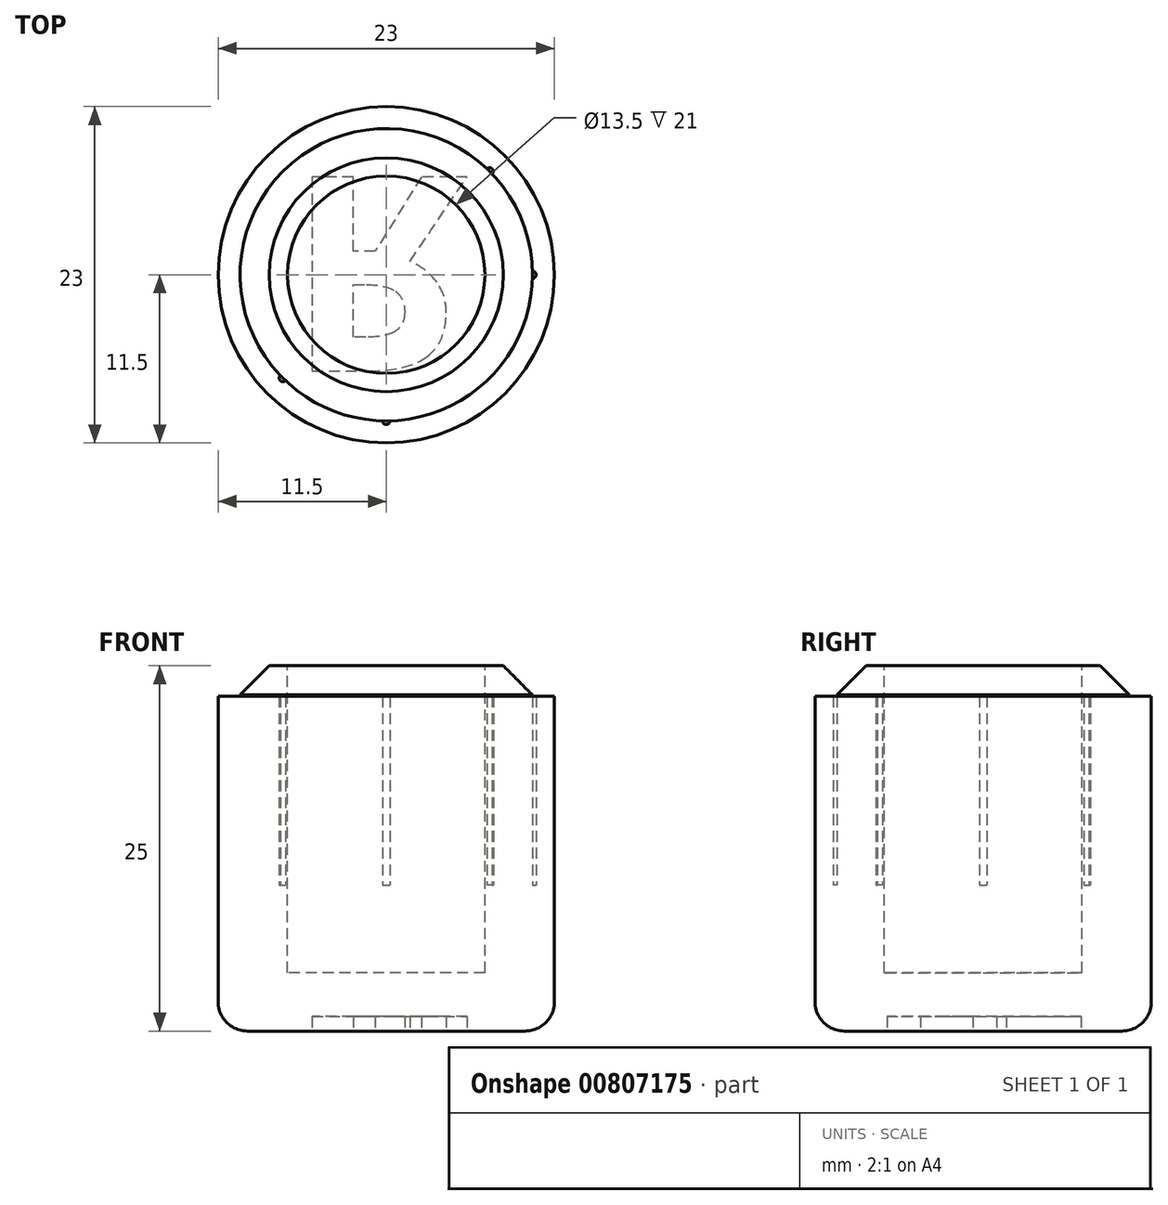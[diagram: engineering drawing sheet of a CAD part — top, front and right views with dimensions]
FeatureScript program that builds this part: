
annotation { "Feature Type Name" : "Feature", "Feature Type Description" : "" }
export const myFeature = defineFeature(function(context is Context, id is Id, definition is map)
    precondition{}
    {
        {
            var Q0;
            Q0=qCreatedBy(makeId("Top.planeOp"),FACE);
            var sketch = newSketch(context, id + "F0", { "sketchPlane" : qUnion([Q0])});
            skCircle(sketch, "E0", {"center": v(0, 0) * mm, "radius": 11.5 * mm});
            skSolve(sketch);
        }
        {
            var Q0;
            Q0 = qSketchRegion(id + "F0", true);
            extrude(context, id + "F1", {"entities" : qUnion([Q0]), "depth" : 10 * mm, "offsetDistance" : 25 * mm});
        }
        {
            var Q0;
            Q0=makeQuery(id+"F1.opExtrude","CAP_FACE",FACE,{"disambiguationData":[OSD([sQuery(id+"F0.wireOp",EDGE,"E0")])],"isStart":false});
            var sketch = newSketch(context, id + "F2", { "sketchPlane" : qUnion([Q0])});
            skCircle(sketch, "E1", {"center": v(0, 0) * mm, "radius": 6.75 * mm});
            skSolve(sketch);
        }
        {
            var Q0;
            Q0 = qSketchRegion(id + "F2", true);
            extrude(context, id + "F3", {"entities" : qUnion([Q0]), "operationType" : NewBodyOperationType.REMOVE, "oppositeDirection" : true, "depth" : 6 * mm, "offsetDistance" : 25 * mm});
        }
        {
            var Q0;
            Q0=makeQuery(id+"F1.opExtrude","CAP_FACE",FACE,{"disambiguationData":[OSD([sQuery(id+"F0.wireOp",EDGE,"E0")])],"isStart":false});
            var sketch = newSketch(context, id + "F4", { "sketchPlane" : qUnion([Q0])});
            skCircle(sketch, "E2", {"center": v(0, 0) * mm, "radius": 6.75 * mm});
            skCircle(sketch, "E3", {"center": v(0, 0) * mm, "radius": 10 * mm});
            skSolve(sketch);
        }
        {
            var Q0;
            Q0=makeQuery(id+"F4.imprint","IMPRINT",FACE,{"disambiguationData":[TD([[makeQuery(id+"F4.imprint","IMPRINT",EDGE,{"derivedFrom":sQuery(id+"F4.wireOp",EDGE,"E2")}),-1.0]])]});
            extrude(context, id + "F5", {"entities" : qUnion([Q0]), "operationType" : NewBodyOperationType.ADD, "depth" : 15 * mm, "offsetDistance" : 25 * mm});
        }
        {
            var Q0;
            Q0=makeQuery(id+"F1.opExtrude","CAP_EDGE",EDGE,{"disambiguationData":[OSD([sQuery(id+"F0.wireOp",EDGE,"E0")])],"isStart":true});
            fillet(context, id + "F6", {"entities" : qUnion([Q0]), "radius" : 2 * mm, "tangentPropagation" : true, "allowEdgeOverflow" : false});
        }
        {
            var Q0;
            Q0=makeQuery(id+"F1.opExtrude","CAP_FACE",FACE,{"disambiguationData":[OSD([sQuery(id+"F0.wireOp",EDGE,"E0")])],"isStart":false});
            var sketch = newSketch(context, id + "F7", { "sketchPlane" : qUnion([Q0])});
            skArc(sketch, "E4", {"start": v(0.25, 10) * mm, "mid": v(0, 10.25) * mm, "end": v(-0.25, 10) * mm});
            skArc(sketch, "E5", {"start": v(-6.9, 7.25) * mm, "mid": v(-7.25, 7.25) * mm, "end": v(-7.25, 6.9) * mm});
            skArc(sketch, "E6", {"start": v(-10, 0.25) * mm, "mid": v(-10.25, 0) * mm, "end": v(-10, -0.25) * mm});
            skArc(sketch, "E7.MirrorCS", {"start": v(6.9, 7.25) * mm, "mid": v(7.25, 7.25) * mm, "end": v(7.25, 6.9) * mm});
            skArc(sketch, "E8.MirrorCS", {"start": v(10, 0.25) * mm, "mid": v(10.25, 0) * mm, "end": v(10, -0.25) * mm});
            skArc(sketch, "E9.MirrorCS", {"start": v(0.25, -10) * mm, "mid": v(0, -10.25) * mm, "end": v(-0.25, -10) * mm});
            skArc(sketch, "E10.MirrorCS", {"start": v(-6.9, -7.25) * mm, "mid": v(-7.25, -7.25) * mm, "end": v(-7.25, -6.9) * mm});
            skArc(sketch, "E11.MirrorCS", {"start": v(6.9, -7.25) * mm, "mid": v(7.25, -7.25) * mm, "end": v(7.25, -6.9) * mm});
            skSolve(sketch);
        }
        {
            var Q0;
            {var subQ0=sQuery(id+"F7.wireOp",EDGE,"E4");Q0=makeQuery(id+"F7.imprint","IMPRINT",FACE,{"disambiguationData":[TD([[makeQuery(id+"F7.imprint","IMPRINT",EDGE,{"derivedFrom":subQ0}),1.0]])]});}
            var Q1;
            {var subQ0=sQuery(id+"F7.wireOp",EDGE,"E7.MirrorCS");Q1=makeQuery(id+"F7.imprint","IMPRINT",FACE,{"disambiguationData":[TD([[makeQuery(id+"F7.imprint","IMPRINT",EDGE,{"derivedFrom":subQ0}),-1.0]])]});}
            var Q2;
            {var subQ0=sQuery(id+"F7.wireOp",EDGE,"E8.MirrorCS");Q2=makeQuery(id+"F7.imprint","IMPRINT",FACE,{"disambiguationData":[TD([[makeQuery(id+"F7.imprint","IMPRINT",EDGE,{"derivedFrom":subQ0}),-1.0]])]});}
            var Q3;
            {var subQ0=sQuery(id+"F7.wireOp",EDGE,"E11.MirrorCS");Q3=makeQuery(id+"F7.imprint","IMPRINT",FACE,{"disambiguationData":[TD([[makeQuery(id+"F7.imprint","IMPRINT",EDGE,{"derivedFrom":subQ0}),1.0]])]});}
            var Q4;
            {var subQ0=sQuery(id+"F7.wireOp",EDGE,"E9.MirrorCS");Q4=makeQuery(id+"F7.imprint","IMPRINT",FACE,{"disambiguationData":[TD([[makeQuery(id+"F7.imprint","IMPRINT",EDGE,{"derivedFrom":subQ0}),-1.0]])]});}
            var Q5;
            {var subQ0=sQuery(id+"F7.wireOp",EDGE,"E10.MirrorCS");Q5=makeQuery(id+"F7.imprint","IMPRINT",FACE,{"disambiguationData":[TD([[makeQuery(id+"F7.imprint","IMPRINT",EDGE,{"derivedFrom":subQ0}),-1.0]])]});}
            var Q6;
            {var subQ0=sQuery(id+"F7.wireOp",EDGE,"E6");Q6=makeQuery(id+"F7.imprint","IMPRINT",FACE,{"disambiguationData":[TD([[makeQuery(id+"F7.imprint","IMPRINT",EDGE,{"derivedFrom":subQ0}),1.0]])]});}
            var Q7;
            {var subQ0=sQuery(id+"F7.wireOp",EDGE,"E5");Q7=makeQuery(id+"F7.imprint","IMPRINT",FACE,{"disambiguationData":[TD([[makeQuery(id+"F7.imprint","IMPRINT",EDGE,{"derivedFrom":subQ0}),1.0]])]});}
            extrude(context, id + "F8", {"entities" : qUnion([Q0, Q1, Q2, Q3, Q4, Q5, Q6, Q7]), "operationType" : NewBodyOperationType.ADD, "depth" : 12.9 * mm, "offsetDistance" : 25 * mm});
        }
        {
            var Q0;
            Q0=makeQuery(id+"F5.opExtrude","CAP_EDGE",EDGE,{"disambiguationData":[OSD([sQuery(id+"F4.wireOp",EDGE,"E3")])],"isStart":false});
            chamfer(context, id + "F9", {"entities" : qUnion([Q0]), "width" : 2 * mm, "tangentPropagation" : true});
        }
        {
            var Q0;
            Q0=makeQuery(id+"F1.opExtrude","CAP_FACE",FACE,{"disambiguationData":[OSD([sQuery(id+"F0.wireOp",EDGE,"E0")])],"isStart":true});
            var sketch = newSketch(context, id + "F10", { "sketchPlane" : qUnion([Q0])});
            skText(sketch, "E12", { "text": "R\n", "fontName": "OpenSans-Bold.ttf"});
            const initialGuessF10  = {"E12": [-0.00674, -0.0067, 1, 0, 0.01339]};
            skSetInitialGuess(sketch, initialGuessF10);
            skSolve(sketch);
        }
        {
            var Q0;
            Q0=makeQuery(id+"F10.imprint","IMPRINT",FACE,{"disambiguationData":[TD([[makeQuery(id+"F10.imprint","IMPRINT",EDGE,{"derivedFrom":sQuery(id+"F10.wireOp",EDGE,"E12.sketch_text.stroke-0")}),-1.0]])]});
            extrude(context, id + "F11", {"entities" : qUnion([Q0]), "operationType" : NewBodyOperationType.REMOVE, "oppositeDirection" : true, "depth" : 1 * mm, "offsetDistance" : 25 * mm});
        }
    });
